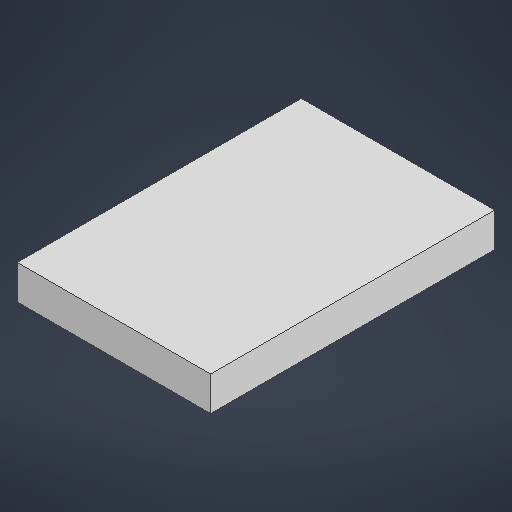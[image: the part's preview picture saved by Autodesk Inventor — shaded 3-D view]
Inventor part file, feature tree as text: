
AUTODESK INVENTOR PART (.ipt)
format: ipt  version: 2025.2 (Build 292293000, 293)  size: 156,672 bytes
history: native  units: mm
features: extrude x1, sketch x1
ambient origin geometry x8: Origin, YZ Plane, XZ Plane, XY Plane, X Axis, Y Axis, Z Axis, Center Point
bodies: Solid1 (feature_tree)
feature tree (2):
  extrude  "Extrusion1"  Depth=56.5mm
  sketch  "Sketch1"  dims[d0=83.0mm d1=56.5mm d2=10.0mm d3=0.0mm]
